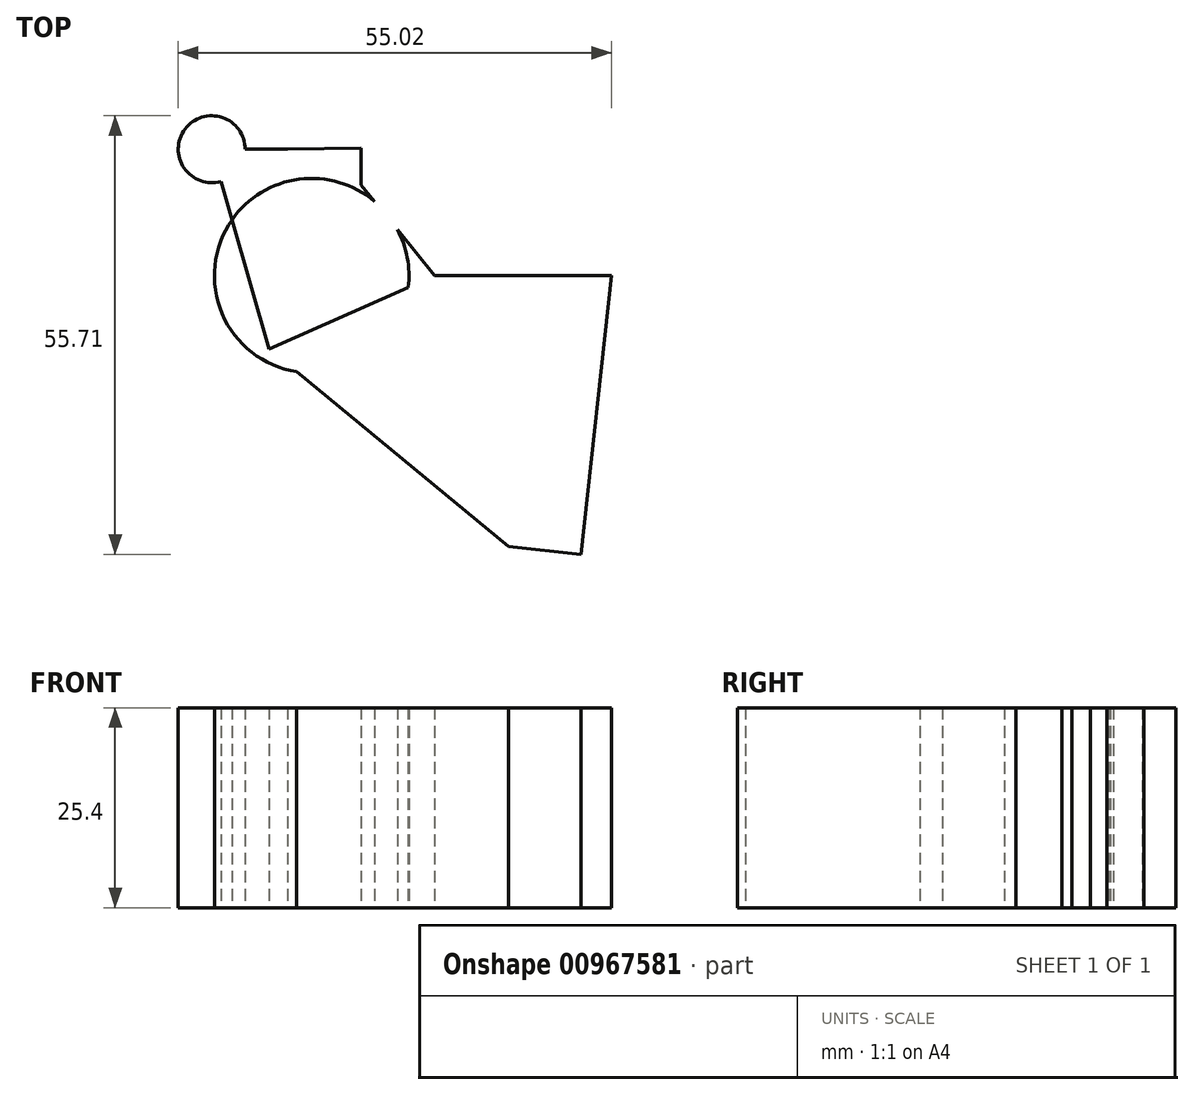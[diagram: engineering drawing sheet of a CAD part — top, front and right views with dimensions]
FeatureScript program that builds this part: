
annotation { "Feature Type Name" : "Feature", "Feature Type Description" : "" }
export const myFeature = defineFeature(function(context is Context, id is Id, definition is map)
    precondition{}
    {
        {
            var Q0;
            Q0=qCreatedBy(makeId("Top.planeOp"),FACE);
            var sketch = newSketch(context, id + "F0", { "sketchPlane" : qUnion([Q0])});
            skLineSegment(sketch, "E0", {"start": v(-3.07, 16.06) * mm, "end": v(6.28, 14.02) * mm});
            skLineSegment(sketch, "E1", {"start": v(6.28, 16.2) * mm, "end": v(6.28, 11.53) * mm});
            skLineSegment(sketch, "E2", {"start": v(6.28, 11.53) * mm, "end": v(15.62, 0) * mm});
            skLineSegment(sketch, "E3", {"start": v(15.62, 0) * mm, "end": v(38.1, 0) * mm});
            skLineSegment(sketch, "E4", {"start": v(38.1, 0.3) * mm, "end": v(34.2, -35.4) * mm});
            skLineSegment(sketch, "E5", {"start": v(34.2, -35.4) * mm, "end": v(24.98, -34.4) * mm});
            skLineSegment(sketch, "E6", {"start": v(17.08, -17.96) * mm, "end": v(15.62, 0) * mm});
            skLineSegment(sketch, "E7", {"start": v(15.62, 0) * mm, "end": v(-5.4, -9.34) * mm});
            skLineSegment(sketch, "E8", {"start": v(-5.4, -9.34) * mm, "end": v(24.98, -34.4) * mm});
            skLineSegment(sketch, "E9", {"start": v(-5.4, -9.34) * mm, "end": v(-12.7, 16.06) * mm});
            skLineSegment(sketch, "E10", {"start": v(-12.7, 16.06) * mm, "end": v(-3.07, 16.06) * mm});
            skCircle(sketch, "E11", {"center": v(-12.7, 16.06) * mm, "radius": 4.25 * mm});
            skCircle(sketch, "E12", {"center": v(0, 0) * mm, "radius": 12.36 * mm});
            skLineSegment(sketch, "E13", {"start": v(6.28, 16.2) * mm, "end": v(-3.07, 16.06) * mm});
            skSolve(sketch);
        }
        {
            var Q0;
            {var subQ0=sQuery(id+"F0.wireOp",EDGE,"E10");var subQ1=sQuery(id+"F0.wireOp",EDGE,"E9");var subQ2=makeQuery(id+"F0.imprint","INTERSECT",VERTEX,{"derivedFrom":[subQ1,subQ0]});Q0=makeQuery(id+"F0.imprint","IMPRINT",FACE,{"disambiguationData":[TD([[makeQuery(id+"F0.imprint","IMPRINT",EDGE,{"disambiguationData":[TD([[subQ2,1.0]])],"derivedFrom":subQ1}),-1.0]])]});}
            var Q1;
            {var subQ0=sQuery(id+"F0.wireOp",EDGE,"E10");var subQ1=sQuery(id+"F0.wireOp",EDGE,"E9");var subQ2=makeQuery(id+"F0.imprint","INTERSECT",VERTEX,{"derivedFrom":[subQ1,subQ0]});Q1=makeQuery(id+"F0.imprint","IMPRINT",FACE,{"disambiguationData":[TD([[makeQuery(id+"F0.imprint","IMPRINT",EDGE,{"disambiguationData":[TD([[subQ2,1.0]])],"derivedFrom":subQ1}),1.0]])]});}
            var Q2;
            {var subQ1=sQuery(id+"F0.wireOp",EDGE,"E8");var subQ3=sQuery(id+"F0.wireOp",EDGE,"E12");var subQ4=makeQuery(id+"F0.imprint","INTERSECT",VERTEX,{"derivedFrom":[subQ1,subQ3]});Q2=makeQuery(id+"F0.imprint","IMPRINT",FACE,{"disambiguationData":[TD([[makeQuery(id+"F0.imprint","IMPRINT",EDGE,{"disambiguationData":[TD([[subQ4,1.0]])],"derivedFrom":subQ3}),1.0]])]});}
            var Q3;
            {var subQ0=sQuery(id+"F0.wireOp",EDGE,"E12");var subQ1=sQuery(id+"F0.wireOp",EDGE,"E2");var subQ2=makeQuery(id+"F0.imprint","INTERSECT",VERTEX,{"disambiguationData":[OD(0.0)],"derivedFrom":[subQ1,subQ0]});Q3=makeQuery(id+"F0.imprint","IMPRINT",FACE,{"disambiguationData":[TD([[makeQuery(id+"F0.imprint","IMPRINT",EDGE,{"disambiguationData":[TD([[subQ2,-1.0]])],"derivedFrom":subQ1}),-1.0]])]});}
            var Q4;
            {var subQ0=sQuery(id+"F0.wireOp",EDGE,"E12");var subQ1=sQuery(id+"F0.wireOp",EDGE,"E2");var subQ2=makeQuery(id+"F0.imprint","INTERSECT",VERTEX,{"disambiguationData":[OD(0.0)],"derivedFrom":[subQ1,subQ0]});Q4=makeQuery(id+"F0.imprint","IMPRINT",FACE,{"disambiguationData":[TD([[makeQuery(id+"F0.imprint","IMPRINT",EDGE,{"disambiguationData":[TD([[subQ2,-1.0]])],"derivedFrom":subQ1}),1.0]])]});}
            var Q5;
            {var subQ0=sQuery(id+"F0.wireOp",EDGE,"E8");var subQ3=sQuery(id+"F0.wireOp",EDGE,"E12");var subQ5=makeQuery(id+"F0.imprint","INTERSECT",VERTEX,{"derivedFrom":[subQ0,subQ3]});Q5=makeQuery(id+"F0.imprint","IMPRINT",FACE,{"disambiguationData":[TD([[makeQuery(id+"F0.imprint","IMPRINT",EDGE,{"disambiguationData":[TD([[subQ5,-1.0]])],"derivedFrom":subQ3}),1.0]])]});}
            var Q6;
            {var subQ9=sQuery(id+"F0.wireOp",EDGE,"E0");Q6=makeQuery(id+"F0.imprint","IMPRINT",FACE,{"disambiguationData":[TD([[makeQuery(id+"F0.imprint","IMPRINT",EDGE,{"derivedFrom":subQ9}),-1.0]])]});}
            var Q7;
            {var subQ0=sQuery(id+"F0.wireOp",EDGE,"E0");Q7=makeQuery(id+"F0.imprint","IMPRINT",FACE,{"disambiguationData":[TD([[makeQuery(id+"F0.imprint","IMPRINT",EDGE,{"derivedFrom":subQ0}),1.0]])]});}
            var Q8;
            {var subQ1=sQuery(id+"F0.wireOp",EDGE,"E2");var subQ3=sQuery(id+"F0.wireOp",EDGE,"E12");var subQ4=makeQuery(id+"F0.imprint","INTERSECT",VERTEX,{"disambiguationData":[OD(1.0)],"derivedFrom":[subQ1,subQ3]});Q8=makeQuery(id+"F0.imprint","IMPRINT",FACE,{"disambiguationData":[TD([[makeQuery(id+"F0.imprint","IMPRINT",EDGE,{"disambiguationData":[TD([[subQ4,1.0]])],"derivedFrom":subQ3}),-1.0]])]});}
            var Q9;
            {var subQ5=sQuery(id+"F0.wireOp",EDGE,"E5");Q9=makeQuery(id+"F0.imprint","IMPRINT",FACE,{"disambiguationData":[TD([[makeQuery(id+"F0.imprint","IMPRINT",EDGE,{"derivedFrom":subQ5}),-1.0]])]});}
            extrude(context, id + "F1", {"entities" : qUnion([Q0, Q1, Q2, Q3, Q4, Q5, Q6, Q7, Q8, Q9]), "depth" : 25.4 * mm, "offsetDistance" : 25.4 * mm});
        }
    });
